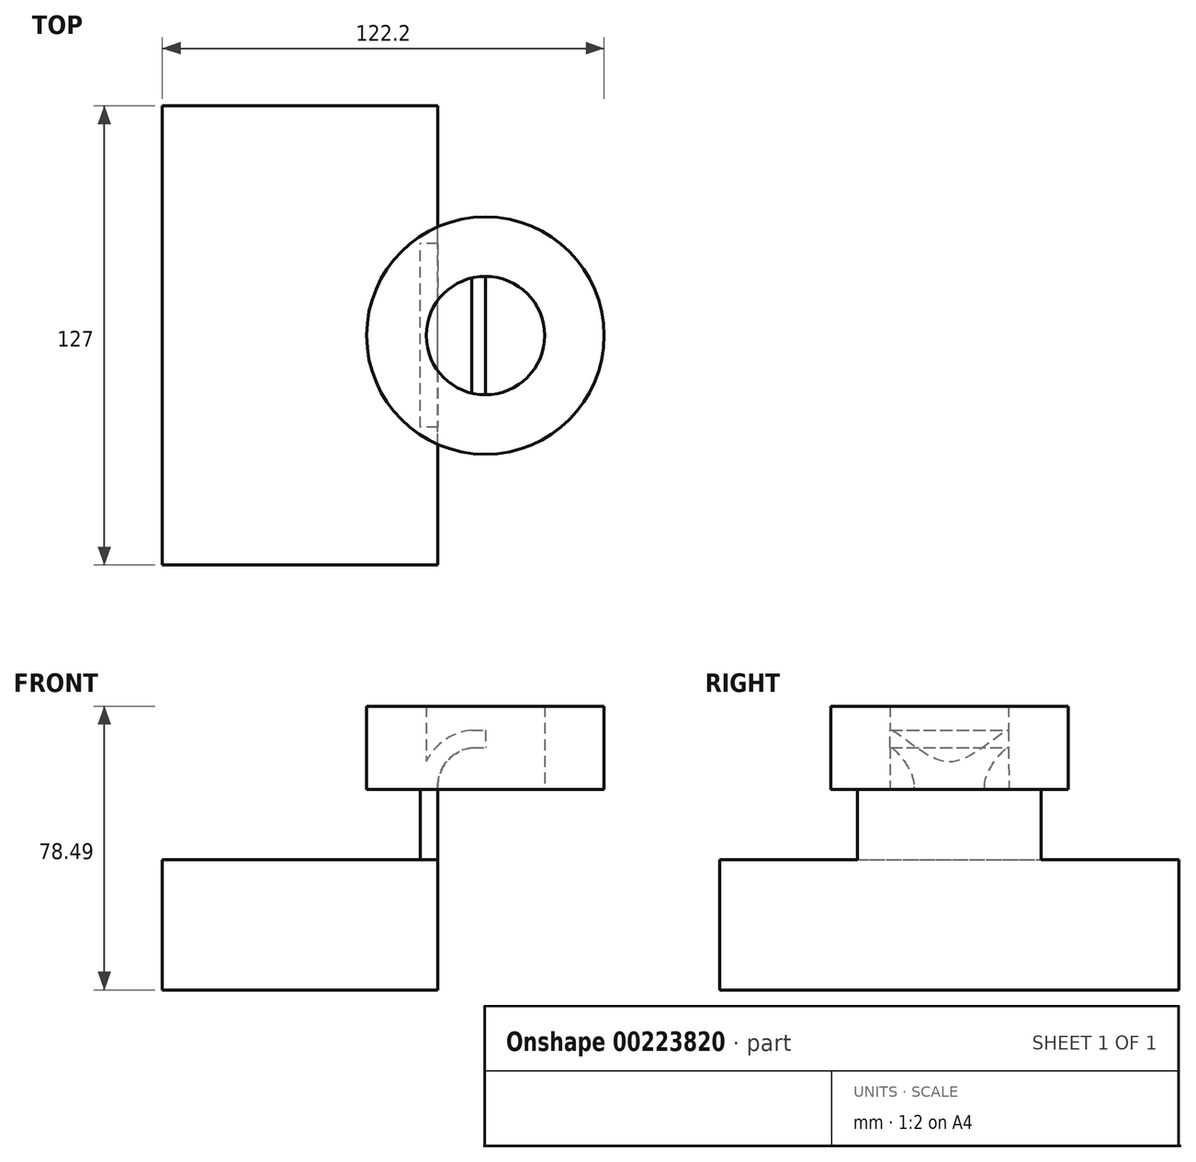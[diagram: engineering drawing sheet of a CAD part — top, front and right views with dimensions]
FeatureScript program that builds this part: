
annotation { "Feature Type Name" : "Feature", "Feature Type Description" : "" }
export const myFeature = defineFeature(function(context is Context, id is Id, definition is map)
    precondition{}
    {
        {
            var Q0;
            Q0=qCreatedBy(makeId("Front.planeOp"),FACE);
            var sketch = newSketch(context, id + "F0", { "sketchPlane" : qUnion([Q0])});
            skLineSegment(sketch, "E0.bottom", {"start": v(-38.08, 18.03) * mm, "end": v(38.08, 18.03) * mm});
            skLineSegment(sketch, "E0.top", {"start": v(-38.08, -18.03) * mm, "end": v(38.08, -18.03) * mm});
            skLineSegment(sketch, "E0.left", {"start": v(-38.08, 18.03) * mm, "end": v(-38.08, -18.03) * mm});
            skLineSegment(sketch, "E0.right", {"start": v(38.08, 18.03) * mm, "end": v(38.08, -18.03) * mm});
            skPoint(sketch, "E0.middle", {"position": v(0, 0) * mm});
            skLineSegment(sketch, "E1.bottom", {"start": v(84.12, 37.48) * mm, "end": v(51.28, 37.48) * mm});
            skLineSegment(sketch, "E1.top", {"start": v(84.12, 60.46) * mm, "end": v(51.28, 60.46) * mm});
            skLineSegment(sketch, "E1.left", {"start": v(84.12, 37.48) * mm, "end": v(84.12, 60.46) * mm});
            skLineSegment(sketch, "E1.right", {"start": v(51.28, 37.48) * mm, "end": v(51.28, 60.46) * mm});
            skPoint(sketch, "E1.middle", {"position": v(67.7, 48.97) * mm});
            skLineSegment(sketch, "E2", {"start": v(38.08, 18.03) * mm, "end": v(38.08, 38.2) * mm});
            skLineSegment(sketch, "E3", {"start": v(67.7, 48.97) * mm, "end": v(47.76, 48.97) * mm});
            skPoint(sketch, "E3.endSnap0", {"position": v(51.28, 48.97) * mm});
            skArc(sketch, "E4", {"start": v(38.08, 38.2) * mm, "mid": v(40.86, 45.44) * mm, "end": v(47.76, 48.97) * mm});
            skLineSegment(sketch, "E5.0", {"start": v(67.65, 53.8) * mm, "end": v(47.53, 53.8) * mm});
            skArc(sketch, "E5.1", {"start": v(33.26, 38.2) * mm, "mid": v(37.36, 48.77) * mm, "end": v(47.53, 53.8) * mm});
            skLineSegment(sketch, "E5.2", {"start": v(33.26, 18.03) * mm, "end": v(33.26, 38.2) * mm});
            skFitSpline(sketch, "E6", {"points": [v(-38.08, 18.03) * mm, v(51.28, 53.8) * mm], "startDerivative": vector(97.28, 2.4) * mm, "endDerivative": vector(76.23, -59) * mm});
            skLineSegment(sketch, "E7", {"start": v(67.7, 37.48) * mm, "end": v(67.65, 60.46) * mm});
            skSolve(sketch);
        }
        {
            var Q0;
            Q0=makeQuery(id+"F0.imprint","IMPRINT",FACE,{"disambiguationData":[TD([[makeQuery(id+"F0.imprint","IMPRINT",EDGE,{"derivedFrom":sQuery(id+"F0.wireOp",EDGE,"E0.top")}),1.0]])]});
            extrude(context, id + "F1", {"entities" : qUnion([Q0]), "endBound" : BoundingType.SYMMETRIC, "depth" : 127 * mm});
        }
        {
            var Q0;
            {var subQ5=sQuery(id+"F0.wireOp",EDGE,"E2");Q0=makeQuery(id+"F0.imprint","IMPRINT",FACE,{"disambiguationData":[TD([[makeQuery(id+"F0.imprint","IMPRINT",EDGE,{"derivedFrom":subQ5}),1.0]])]});}
            extrude(context, id + "F2", {"entities" : qUnion([Q0]), "operationType" : NewBodyOperationType.ADD, "endBound" : BoundingType.SYMMETRIC, "depth" : 50.8 * mm});
        }
        {
            var Q0;
            {var subQ0=sQuery(id+"F0.wireOp",EDGE,"E5.1");Q0=makeQuery(id+"F0.imprint","IMPRINT",FACE,{"disambiguationData":[TD([[makeQuery(id+"F0.imprint","IMPRINT",EDGE,{"derivedFrom":subQ0}),1.0]])]});}
            extrude(context, id + "F3", {"entities" : qUnion([Q0]), "operationType" : NewBodyOperationType.ADD, "endBound" : BoundingType.SYMMETRIC, "depth" : 25.4 * mm});
        }
        {
            var Q0;
            {var subQ0=sQuery(id+"F0.wireOp",EDGE,"E1.left");Q0=makeQuery(id+"F0.imprint","IMPRINT",FACE,{"disambiguationData":[TD([[makeQuery(id+"F0.imprint","IMPRINT",EDGE,{"derivedFrom":subQ0}),1.0]])]});}
            var Q1;
            Q1=sQuery(id+"F0.wireOp",EDGE,"E1.right");
            revolve(context, id + "F4", {"operationType" : NewBodyOperationType.ADD, "entities" : qUnion([Q0]), "axis" : qUnion([Q1]), "revolveType" : RevolveType.FULL});
        }
    });
